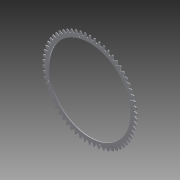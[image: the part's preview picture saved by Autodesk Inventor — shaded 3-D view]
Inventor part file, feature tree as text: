
AUTODESK INVENTOR PART (.ipt)
format: ipt  version: 2014 SP1 (Build 180222100, 222)  size: 516,608 bytes
history: native  units: in
note: dims shown in document units (in); Inventor stores cm internally (conversion verified against a paired STEP export)
features: reference x5, extrude x3, sketch x3
ambient origin geometry x8: Origin, YZ Plane, XZ Plane, XY Plane, X Axis, Y Axis, Z Axis, Center Point
bodies: Solid1 (feature_tree)
feature tree (11):
  extrude  "Extrusion1"  Depth=0.125in TaperAngle=0.0deg
  extrude  "Extrusion2"  [1 undecoded]
  extrude  "Extrusion3"  [1 undecoded]
  sketch  "Sketch1"  dims[d0=0.125in d1=0.0in d2=1.0in d3=0.0in]
  sketch  "Sketch2"  dims[d4=1.0in d5=0.0in]
  reference  "Reference1"
  sketch  "Sketch3"
  reference  "Reference2"
  reference  "Reference3"
  reference  "Reference4"
  reference  "Reference5"
note: 2 required parameter values undecoded (feature->parameter linkage not recoverable at this tier; creation-order binding heuristic only, values carry confidence <= 0.55)
